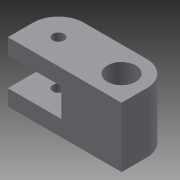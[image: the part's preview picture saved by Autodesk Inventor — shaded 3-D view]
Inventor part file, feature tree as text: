
AUTODESK INVENTOR PART (.ipt)
format: ipt  version: 2015 (Build 190159000, 159)  size: 119,296 bytes
history: native  units: mm
features: sketch x4, hole x2, extrude x1, plane x1, other x1, revolve x1
ambient origin geometry x8: Origin, YZ Plane, XZ Plane, XY Plane, X Axis, Y Axis, Z Axis, Center Point
bodies: Solid1 (feature_tree)
feature tree (10):
  extrude  "Extrusion1"  Depth=36.0mm
  hole  "Hole1"  [1 undecoded]
  hole  "Hole2"  [1 undecoded]
  plane  "Work Plane1"
  other  "Work Axis1"
  revolve  "Revolution2"  [1 undecoded]
  sketch  "Sketch1"  dims[d0=16.0mm d2=36.0mm]
  sketch  "Sketch2"  dims[d3=19.0mm d4=0.0mm d5=8.0mm]
  sketch  "Sketch3"  dims[d6=8.0mm]
  sketch  "Sketch7"  dims[d9=3.6mm d10=6.0mm d11=4.0mm d12=2.0mm d13=90.0deg d14=8.0mm d15=20.594885mm d16=8.0mm d17=8.0mm d18=9.0mm d19=6.0mm d20=4.0mm d21=2.0mm d22=90.0deg d23=8.0mm d24=20.594885mm d32=12.0mm d34=9.5mm d35=9.0mm d36=90.0deg]
note: 3 required parameter values undecoded (feature->parameter linkage not recoverable at this tier; creation-order binding heuristic only, values carry confidence <= 0.55)